# Revit family: CENTUM Isoliersattel für Rollenlager
name_source: partatom
category: HLS-Bauteile
revit_build: Autodesk Revit 2017 (Build: 20190507_1515(x64)
units: mm (PartAtom-declared; Revit-internal decimal feet)

## family parameters
Arbeitsebenenbasiert = Ja
Beim Laden mit Abzugskörper schneiden = Nein
Bemaßung runder Anschluss = Durchmesser verwenden
Gemeinsam genutzt = Ja
Immer vertikal = Nein
Raumberechnungspunkt = Nein
Teiletyp = Normal

## types (150) — shared parameters
Bauart = Auflagesattel
Fabrikat = MEFA
Firma = MEFA Befestigungs- und Montagesysteme GmbH
Isoliersattel = MEFA Isoliersattel 508 Isolierstärke  80
Länge Unterbau = 300 mm
Material = Stahl
Materialname = S235
Mengeneinheit = St
Verschluss = Mutter / Verschluss-Schraube
Vorgabe-Ansicht = 1219 mm
vpe = 1 St

## per-type parameters (varying)
| type | Artikelnummer | Breite Schellenband | Durchmesser Rollenauflage | EAN | Gewicht | Gewicht pro Bauteil | Kurztext1 | Kurztext2 | Oberflaeche | Rohraußendurchmesser | Stärke Material | Stärke Schellenband | Verschluss-Schraube | für Dämmstärke |
| CENTUM Isoliersattel für Rollenlager 219 Iso  50, fvz | 149afae0219 | 60 mm | 320 mm | 4250928433459 | 9.87 kg | 9.87 kg | Isoliersattel 219 60 x 6 mm | für Iso 50 mm fsv | feuerstückverzinkt | 219 mm  [stored 0.718504 ft] | 6 mm  [stored 0.019685 ft] | 6 mm | M16x60 | 50 mm |
| CENTUM Isoliersattel für Rollenlager 219 Iso  50, gvz | 149agae0219 | 60 mm | 320 mm | 4250928433954 | 9.29 kg | 9.29 kg | Isoliersattel 219 60 x 6 mm | für Iso 50 mm gvz | galvanisch verzinkt | 219 mm  [stored 0.718504 ft] | 6 mm  [stored 0.019685 ft] | 6 mm | M16x55 | 50 mm |
| CENTUM Isoliersattel für Rollenlager 219 Iso  50, roh | 149arae0219 | 60 mm | 320 mm | 4250928434456 | 9.29 kg | 9.29 kg | Isoliersattel 219 60 x 6 mm | für Iso 50 mm roh | roh | 219 mm  [stored 0.718504 ft] | 6 mm  [stored 0.019685 ft] | 6 mm | M16x55 | 50 mm |
| CENTUM Isoliersattel für Rollenlager 219 Iso  80, fvz | 149afah0219 | 60 mm | 380 mm | 4250928433558 | 11.30 kg | 11.30 kg | Isoliersattel 219 60 x 6 mm | für Iso 80 mm fsv | feuerstückverzinkt | 219 mm  [stored 0.718504 ft] | 6 mm  [stored 0.019685 ft] | 6 mm | M16x60 | 80 mm |
| CENTUM Isoliersattel für Rollenlager 219 Iso  80, gvz | 149agah0219 | 60 mm | 380 mm | 4250928434050 | 10.65 kg | 10.65 kg | Isoliersattel 219 60 x 6 mm | für Iso 80 mm gvz | galvanisch verzinkt | 219 mm  [stored 0.718504 ft] | 6 mm  [stored 0.019685 ft] | 6 mm | M16x55 | 80 mm |
| CENTUM Isoliersattel für Rollenlager 219 Iso  80, roh | 149arah0219 | 60 mm | 380 mm | 4250928434555 | 10.65 kg | 10.65 kg | Isoliersattel 219 60 x 6 mm | für Iso 80 mm roh | roh | 219 mm  [stored 0.718504 ft] | 6 mm  [stored 0.019685 ft] | 6 mm | M16x55 | 80 mm |
| CENTUM Isoliersattel für Rollenlager 219 Iso 100, fvz | 149afak0219 | 60 mm | 420 mm | 4250928433657 | 12.26 kg | 12.26 kg | Isoliersattel 219 60 x 6 mm | für Iso 100 mm fsv | feuerstückverzinkt | 219 mm  [stored 0.718504 ft] | 6 mm  [stored 0.019685 ft] | 6 mm | M16x60 | 100 mm |
| CENTUM Isoliersattel für Rollenlager 219 Iso 100, gvz | 149agak0219 | 60 mm | 420 mm | 4250928434159 | 11.55 kg | 11.55 kg | Isoliersattel 219 60 x 6 mm | für Iso 100 mm gvz | galvanisch verzinkt | 219 mm  [stored 0.718504 ft] | 6 mm  [stored 0.019685 ft] | 6 mm | M16x55 | 100 mm |
| CENTUM Isoliersattel für Rollenlager 219 Iso 100, roh | 149arak0219 | 60 mm | 420 mm | 4250928434654 | 11.55 kg | 11.55 kg | Isoliersattel 219 60 x 6 mm | für Iso 100 mm roh | roh | 219 mm  [stored 0.718504 ft] | 6 mm  [stored 0.019685 ft] | 6 mm | M16x55 | 100 mm |
| CENTUM Isoliersattel für Rollenlager 219 Iso 120, fvz | 149afam0219 | 60 mm | 460 mm | 4250928433756 | 13.22 kg | 13.22 kg | Isoliersattel 219 60 x 6 mm | für Iso 120 mm fsv | feuerstückverzinkt | 219 mm  [stored 0.718504 ft] | 6 mm  [stored 0.019685 ft] | 6 mm | M16x60 | 120 mm |
| CENTUM Isoliersattel für Rollenlager 219 Iso 120, gvz | 149agam0219 | 60 mm | 460 mm | 4250928434258 | 12.45 kg | 12.45 kg | Isoliersattel 219 60 x 6 mm | für Iso 120 mm gvz | galvanisch verzinkt | 219 mm  [stored 0.718504 ft] | 6 mm  [stored 0.019685 ft] | 6 mm | M16x55 | 120 mm |
| CENTUM Isoliersattel für Rollenlager 219 Iso 120, roh | 149aram0219 | 60 mm | 460 mm | 4250928434753 | 12.45 kg | 12.45 kg | Isoliersattel 219 60 x 6 mm | für Iso 120 mm roh | roh | 219 mm  [stored 0.718504 ft] | 6 mm  [stored 0.019685 ft] | 6 mm | M16x55 | 120 mm |
| CENTUM Isoliersattel für Rollenlager 219 Iso 150, fvz | 149afap0219 | 60 mm | 520 mm | 4250928433855 | 14.66 kg | 14.66 kg | Isoliersattel 219 60 x 6 mm | für Iso 150 mm fsv | feuerstückverzinkt | 219 mm  [stored 0.718504 ft] | 6 mm  [stored 0.019685 ft] | 6 mm | M16x60 | 150 mm |
| CENTUM Isoliersattel für Rollenlager 219 Iso 150, gvz | 149agap0219 | 60 mm | 520 mm | 4250928434357 | 13.82 kg | 13.82 kg | Isoliersattel 219 60 x 6 mm | für Iso 150 mm gvz | galvanisch verzinkt | 219 mm  [stored 0.718504 ft] | 6 mm  [stored 0.019685 ft] | 6 mm | M16x55 | 150 mm |
| CENTUM Isoliersattel für Rollenlager 219 Iso 150, roh | 149arap0219 | 60 mm | 520 mm | 4250928434852 | 13.82 kg | 13.82 kg | Isoliersattel 219 60 x 6 mm | für Iso 150 mm roh | roh | 219 mm  [stored 0.718504 ft] | 6 mm  [stored 0.019685 ft] | 6 mm | M16x55 | 150 mm |
| CENTUM Isoliersattel für Rollenlager 273 Iso  50, fvz | 149afae0273 | 60 mm | 375 mm | 4250928433466 | 12.61 kg | 12.61 kg | Isoliersattel 273 60 x 6 mm | für Iso 50 mm fsv | feuerstückverzinkt | 273 mm  [stored 0.895669 ft] | 8 mm  [stored 0.0262467 ft] | 6 mm | M16x60 | 50 mm |
| CENTUM Isoliersattel für Rollenlager 273 Iso  50, gvz | 149agae0273 | 60 mm | 375 mm | 4250928433961 | 11.95 kg | 11.95 kg | Isoliersattel 273 60 x 6 mm | für Iso 50 mm gvz | galvanisch verzinkt | 273 mm  [stored 0.895669 ft] | 8 mm  [stored 0.0262467 ft] | 6 mm | M16x55 | 50 mm |
| CENTUM Isoliersattel für Rollenlager 273 Iso  50, roh | 149arae0273 | 60 mm | 375 mm | 4250928434463 | 11.95 kg | 11.95 kg | Isoliersattel 273 60 x 6 mm | für Iso 50 mm roh | roh | 273 mm  [stored 0.895669 ft] | 8 mm  [stored 0.0262467 ft] | 6 mm | M16x55 | 50 mm |
| CENTUM Isoliersattel für Rollenlager 273 Iso  80, fvz | 149afah0273 | 60 mm | 435 mm | 4250928433565 | 14.51 kg | 14.51 kg | Isoliersattel 273 60 x 6 mm | für Iso 80 mm fsv | feuerstückverzinkt | 273 mm  [stored 0.895669 ft] | 8 mm  [stored 0.0262467 ft] | 6 mm | M16x60 | 80 mm |
| CENTUM Isoliersattel für Rollenlager 273 Iso  80, gvz | 149agah0273 | 60 mm | 435 mm | 4250928434067 | 13.76 kg | 13.76 kg | Isoliersattel 273 60 x 6 mm | für Iso 80 mm gvz | galvanisch verzinkt | 273 mm  [stored 0.895669 ft] | 8 mm  [stored 0.0262467 ft] | 6 mm | M16x55 | 80 mm |
| CENTUM Isoliersattel für Rollenlager 273 Iso  80, roh | 149arah0273 | 60 mm | 435 mm | 4250928434562 | 13.76 kg | 13.76 kg | Isoliersattel 273 60 x 6 mm | für Iso 80 mm roh | roh | 273 mm  [stored 0.895669 ft] | 8 mm  [stored 0.0262467 ft] | 6 mm | M16x55 | 80 mm |
| CENTUM Isoliersattel für Rollenlager 273 Iso 100, fvz | 149afak0273 | 60 mm | 475 mm | 4250928433664 | 15.78 kg | 15.78 kg | Isoliersattel 273 60 x 6 mm | für Iso 100 mm fsv | feuerstückverzinkt | 273 mm  [stored 0.895669 ft] | 8 mm  [stored 0.0262467 ft] | 6 mm | M16x60 | 100 mm |
| CENTUM Isoliersattel für Rollenlager 273 Iso 100, gvz | 149agak0273 | 60 mm | 475 mm | 4250928434166 | 14.98 kg | 14.98 kg | Isoliersattel 273 60 x 6 mm | für Iso 100 mm gvz | galvanisch verzinkt | 273 mm  [stored 0.895669 ft] | 8 mm  [stored 0.0262467 ft] | 6 mm | M16x55 | 100 mm |
| CENTUM Isoliersattel für Rollenlager 273 Iso 100, roh | 149arak0273 | 60 mm | 475 mm | 4250928434661 | 14.98 kg | 14.98 kg | Isoliersattel 273 60 x 6 mm | für Iso 100 mm roh | roh | 273 mm  [stored 0.895669 ft] | 8 mm  [stored 0.0262467 ft] | 6 mm | M16x55 | 100 mm |
| CENTUM Isoliersattel für Rollenlager 273 Iso 120, fvz | 149afam0273 | 60 mm | 515 mm | 4250928433763 | 17.04 kg | 17.04 kg | Isoliersattel 273 60 x 6 mm | für Iso 120 mm fsv | feuerstückverzinkt | 273 mm  [stored 0.895669 ft] | 8 mm  [stored 0.0262467 ft] | 6 mm | M16x60 | 120 mm |
| CENTUM Isoliersattel für Rollenlager 273 Iso 120, gvz | 149agam0273 | 60 mm | 515 mm | 4250928434265 | 16.19 kg | 16.19 kg | Isoliersattel 273 60 x 6 mm | für Iso 120 mm gvz | galvanisch verzinkt | 273 mm  [stored 0.895669 ft] | 8 mm  [stored 0.0262467 ft] | 6 mm | M16x55 | 120 mm |
| CENTUM Isoliersattel für Rollenlager 273 Iso 120, roh | 149aram0273 | 60 mm | 515 mm | 4250928434760 | 16.19 kg | 16.19 kg | Isoliersattel 273 60 x 6 mm | für Iso 120 mm roh | roh | 273 mm  [stored 0.895669 ft] | 8 mm  [stored 0.0262467 ft] | 6 mm | M16x55 | 120 mm |
| CENTUM Isoliersattel für Rollenlager 273 Iso 150, fvz | 149afap0273 | 60 mm | 575 mm | 4250928433862 | 18.92 kg | 18.92 kg | Isoliersattel 273 60 x 6 mm | für Iso 150 mm fsv | feuerstückverzinkt | 273 mm  [stored 0.895669 ft] | 8 mm  [stored 0.0262467 ft] | 6 mm | M16x60 | 150 mm |
| CENTUM Isoliersattel für Rollenlager 273 Iso 150, gvz | 149agap0273 | 60 mm | 575 mm | 4250928434364 | 17.98 kg | 17.98 kg | Isoliersattel 273 60 x 6 mm | für Iso 150 mm gvz | galvanisch verzinkt | 273 mm  [stored 0.895669 ft] | 8 mm  [stored 0.0262467 ft] | 6 mm | M16x55 | 150 mm |
| CENTUM Isoliersattel für Rollenlager 273 Iso 150, roh | 149arap0273 | 60 mm | 575 mm | 4250928434869 | 17.98 kg | 17.98 kg | Isoliersattel 273 60 x 6 mm | für Iso 150 mm roh | roh | 273 mm  [stored 0.895669 ft] | 8 mm  [stored 0.0262467 ft] | 6 mm | M16x55 | 150 mm |
| CENTUM Isoliersattel für Rollenlager 324 Iso  50, fvz | 149afae0324 | 60 mm | 425 mm | 4250928433473 | 15.42 kg | 15.42 kg | Isoliersattel 324 60 x 6 mm | für Iso 50 mm fsv | feuerstückverzinkt | 324 mm  [stored 1.06299 ft] | 10 mm  [stored 0.0328084 ft] | 6 mm | M16x60 | 50 mm |
| CENTUM Isoliersattel für Rollenlager 324 Iso  50, gvz | 149agae0324 | 60 mm | 425 mm | 4250928433978 | 14.68 kg | 14.68 kg | Isoliersattel 324 60 x 6 mm | für Iso 50 mm gvz | galvanisch verzinkt | 324 mm  [stored 1.06299 ft] | 10 mm  [stored 0.0328084 ft] | 6 mm | M16x55 | 50 mm |
| CENTUM Isoliersattel für Rollenlager 324 Iso  50, roh | 149arae0324 | 60 mm | 425 mm | 4250928434470 | 14.68 kg | 14.68 kg | Isoliersattel 324 60 x 6 mm | für Iso 50 mm roh | roh | 324 mm  [stored 1.06299 ft] | 10 mm  [stored 0.0328084 ft] | 6 mm | M16x55 | 50 mm |
| CENTUM Isoliersattel für Rollenlager 324 Iso  80, fvz | 149afah0324 | 60 mm | 485 mm | 4250928433572 | 17.77 kg | 17.77 kg | Isoliersattel 324 60 x 6 mm | für Iso 80 mm fsv | feuerstückverzinkt | 324 mm  [stored 1.06299 ft] | 10 mm  [stored 0.0328084 ft] | 6 mm | M16x60 | 80 mm |
| CENTUM Isoliersattel für Rollenlager 324 Iso  80, gvz | 149agah0324 | 60 mm | 485 mm | 4250928434074 | 16.95 kg | 16.95 kg | Isoliersattel 324 60 x 6 mm | für Iso 80 mm gvz | galvanisch verzinkt | 324 mm  [stored 1.06299 ft] | 10 mm  [stored 0.0328084 ft] | 6 mm | M16x55 | 80 mm |
| CENTUM Isoliersattel für Rollenlager 324 Iso  80, roh | 149arah0324 | 60 mm | 485 mm | 4250928434579 | 16.95 kg | 16.95 kg | Isoliersattel 324 60 x 6 mm | für Iso 80 mm roh | roh | 324 mm  [stored 1.06299 ft] | 10 mm  [stored 0.0328084 ft] | 6 mm | M16x55 | 80 mm |
| CENTUM Isoliersattel für Rollenlager 324 Iso 100, fvz | 149afak0324 | 60 mm | 525 mm | 4250928433671 | 19.33 kg | 19.33 kg | Isoliersattel 324 60 x 6 mm | für Iso 100 mm fsv | feuerstückverzinkt | 324 mm  [stored 1.06299 ft] | 10 mm  [stored 0.0328084 ft] | 6 mm | M16x60 | 100 mm |
| CENTUM Isoliersattel für Rollenlager 324 Iso 100, gvz | 149agak0324 | 60 mm | 525 mm | 4250928434173 | 18.48 kg | 18.48 kg | Isoliersattel 324 60 x 6 mm | für Iso 100 mm gvz | galvanisch verzinkt | 324 mm  [stored 1.06299 ft] | 10 mm  [stored 0.0328084 ft] | 6 mm | M16x55 | 100 mm |
| CENTUM Isoliersattel für Rollenlager 324 Iso 100, roh | 149arak0324 | 60 mm | 525 mm | 4250928434678 | 18.48 kg | 18.48 kg | Isoliersattel 324 60 x 6 mm | für Iso 100 mm roh | roh | 324 mm  [stored 1.06299 ft] | 10 mm  [stored 0.0328084 ft] | 6 mm | M16x55 | 100 mm |
| CENTUM Isoliersattel für Rollenlager 324 Iso 120, fvz | 149afam0324 | 60 mm | 565 mm | 4250928433770 | 20.90 kg | 20.90 kg | Isoliersattel 324 60 x 6 mm | für Iso 120 mm fsv | feuerstückverzinkt | 324 mm  [stored 1.06299 ft] | 10 mm  [stored 0.0328084 ft] | 6 mm | M16x60 | 120 mm |
| CENTUM Isoliersattel für Rollenlager 324 Iso 120, gvz | 149agam0324 | 60 mm | 565 mm | 4250928434272 | 19.96 kg | 19.96 kg | Isoliersattel 324 60 x 6 mm | für Iso 120 mm gvz | galvanisch verzinkt | 324 mm  [stored 1.06299 ft] | 10 mm  [stored 0.0328084 ft] | 6 mm | M16x55 | 120 mm |
| CENTUM Isoliersattel für Rollenlager 324 Iso 120, roh | 149aram0324 | 60 mm | 565 mm | 4250928434777 | 19.96 kg | 19.96 kg | Isoliersattel 324 60 x 6 mm | für Iso 120 mm roh | roh | 324 mm  [stored 1.06299 ft] | 10 mm  [stored 0.0328084 ft] | 6 mm | M16x55 | 120 mm |
| CENTUM Isoliersattel für Rollenlager 324 Iso 150, fvz | 149afap0324 | 60 mm | 625 mm | 4250928433879 | 23.24 kg | 23.24 kg | Isoliersattel 324 60 x 6 mm | für Iso 150 mm fsv | feuerstückverzinkt | 324 mm  [stored 1.06299 ft] | 10 mm  [stored 0.0328084 ft] | 6 mm | M16x60 | 150 mm |
| CENTUM Isoliersattel für Rollenlager 324 Iso 150, gvz | 149agap0324 | 60 mm | 625 mm | 4250928434371 | 22.23 kg | 22.23 kg | Isoliersattel 324 60 x 6 mm | für Iso 150 mm gvz | galvanisch verzinkt | 324 mm  [stored 1.06299 ft] | 10 mm  [stored 0.0328084 ft] | 6 mm | M16x55 | 150 mm |
| CENTUM Isoliersattel für Rollenlager 324 Iso 150, roh | 149arap0324 | 60 mm | 625 mm | 4250928434876 | 22.23 kg | 22.23 kg | Isoliersattel 324 60 x 6 mm | für Iso 150 mm roh | roh | 324 mm  [stored 1.06299 ft] | 10 mm  [stored 0.0328084 ft] | 6 mm | M16x55 | 150 mm |
| CENTUM Isoliersattel für Rollenlager 356 Iso  50, fvz | 149afae0356 | 60 mm | 460 mm | 4250928433480 | 20.41 kg | 20.41 kg | Isoliersattel 356 60 x 8 mm | für Iso 50 mm fsv | feuerstückverzinkt | 356 mm  [stored 1.16798 ft] | 12 mm  [stored 0.0393701 ft] | 8 mm | M16x60 | 50 mm |
| CENTUM Isoliersattel für Rollenlager 356 Iso  50, gvz | 149agae0356 | 60 mm | 460 mm | 4250928433985 | 19.59 kg | 19.59 kg | Isoliersattel 356 60 x 8 mm | für Iso 50 mm gvz | galvanisch verzinkt | 356 mm  [stored 1.16798 ft] | 12 mm  [stored 0.0393701 ft] | 8 mm | M16x55 | 50 mm |
| CENTUM Isoliersattel für Rollenlager 356 Iso  50, roh | 149arae0356 | 60 mm | 460 mm | 4250928434487 | 19.59 kg | 19.59 kg | Isoliersattel 356 60 x 8 mm | für Iso 50 mm roh | roh | 356 mm  [stored 1.16798 ft] | 12 mm  [stored 0.0393701 ft] | 8 mm | M16x55 | 50 mm |
| CENTUM Isoliersattel für Rollenlager 356 Iso  80, fvz | 149afah0356 | 60 mm | 520 mm | 4250928433589 | 23.21 kg | 23.21 kg | Isoliersattel 356 60 x 8 mm | für Iso 80 mm fsv | feuerstückverzinkt | 356 mm  [stored 1.16798 ft] | 12 mm  [stored 0.0393701 ft] | 8 mm | M16x60 | 80 mm |
| CENTUM Isoliersattel für Rollenlager 356 Iso  80, gvz | 149agah0356 | 60 mm | 520 mm | 4250928434081 | 22.31 kg | 22.31 kg | Isoliersattel 356 60 x 8 mm | für Iso 80 mm gvz | galvanisch verzinkt | 356 mm  [stored 1.16798 ft] | 12 mm  [stored 0.0393701 ft] | 8 mm | M16x55 | 80 mm |
| CENTUM Isoliersattel für Rollenlager 356 Iso  80, roh | 149arah0356 | 60 mm | 520 mm | 4250928434586 | 22.31 kg | 22.31 kg | Isoliersattel 356 60 x 8 mm | für Iso 80 mm roh | roh | 356 mm  [stored 1.16798 ft] | 12 mm  [stored 0.0393701 ft] | 8 mm | M16x55 | 80 mm |
| CENTUM Isoliersattel für Rollenlager 356 Iso 100, fvz | 149afak0356 | 60 mm | 560 mm | 4250928433688 | 25.08 kg | 25.08 kg | Isoliersattel 356 60 x 8 mm | für Iso 100 mm fsv | feuerstückverzinkt | 356 mm  [stored 1.16798 ft] | 12 mm  [stored 0.0393701 ft] | 8 mm | M16x60 | 100 mm |
| CENTUM Isoliersattel für Rollenlager 356 Iso 100, gvz | 149agak0356 | 60 mm | 560 mm | 4250928434180 | 24.13 kg | 24.13 kg | Isoliersattel 356 60 x 8 mm | für Iso 100 mm gvz | galvanisch verzinkt | 356 mm  [stored 1.16798 ft] | 12 mm  [stored 0.0393701 ft] | 8 mm | M16x55 | 100 mm |
| CENTUM Isoliersattel für Rollenlager 356 Iso 100, roh | 149arak0356 | 60 mm | 560 mm | 4250928434685 | 24.13 kg | 24.13 kg | Isoliersattel 356 60 x 8 mm | für Iso 100 mm roh | roh | 356 mm  [stored 1.16798 ft] | 12 mm  [stored 0.0393701 ft] | 8 mm | M16x55 | 100 mm |
| CENTUM Isoliersattel für Rollenlager 356 Iso 120, fvz | 149afam0356 | 60 mm | 600 mm | 4250928433787 | 26.94 kg | 26.94 kg | Isoliersattel 356 60 x 8 mm | für Iso 120 mm fsv | feuerstückverzinkt | 356 mm  [stored 1.16798 ft] | 12 mm  [stored 0.0393701 ft] | 8 mm | M16x60 | 120 mm |
| CENTUM Isoliersattel für Rollenlager 356 Iso 120, gvz | 149agam0356 | 60 mm | 600 mm | 4250928434289 | 25.93 kg | 25.93 kg | Isoliersattel 356 60 x 8 mm | für Iso 120 mm gvz | galvanisch verzinkt | 356 mm  [stored 1.16798 ft] | 12 mm  [stored 0.0393701 ft] | 8 mm | M16x55 | 120 mm |
| CENTUM Isoliersattel für Rollenlager 356 Iso 120, roh | 149aram0356 | 60 mm | 600 mm | 4250928434784 | 25.93 kg | 25.93 kg | Isoliersattel 356 60 x 8 mm | für Iso 120 mm roh | roh | 356 mm  [stored 1.16798 ft] | 12 mm  [stored 0.0393701 ft] | 8 mm | M16x55 | 120 mm |
| CENTUM Isoliersattel für Rollenlager 356 Iso 150, fvz | 149afap0356 | 60 mm | 660 mm | 4250928433886 | 29.74 kg | 29.74 kg | Isoliersattel 356 60 x 8 mm | für Iso 150 mm fsv | feuerstückverzinkt | 356 mm  [stored 1.16798 ft] | 12 mm  [stored 0.0393701 ft] | 8 mm | M16x60 | 150 mm |
| CENTUM Isoliersattel für Rollenlager 356 Iso 150, gvz | 149agap0356 | 60 mm | 660 mm | 4250928434388 | 28.65 kg | 28.65 kg | Isoliersattel 356 60 x 8 mm | für Iso 150 mm gvz | galvanisch verzinkt | 356 mm  [stored 1.16798 ft] | 12 mm  [stored 0.0393701 ft] | 8 mm | M16x55 | 150 mm |
| CENTUM Isoliersattel für Rollenlager 356 Iso 150, roh | 149arap0356 | 60 mm | 660 mm | 4250928434883 | 28.65 kg | 28.65 kg | Isoliersattel 356 60 x 8 mm | für Iso 150 mm roh | roh | 356 mm  [stored 1.16798 ft] | 12 mm  [stored 0.0393701 ft] | 8 mm | M16x55 | 150 mm |
| CENTUM Isoliersattel für Rollenlager 406 Iso  50, fvz | 149afae0406 | 60 mm | 510 mm | 4250928433497 | 22.54 kg | 22.54 kg | Isoliersattel 406 60 x 8 mm | für Iso 50 mm fsv | feuerstückverzinkt | 406 mm  [stored 1.33202 ft] | 12 mm  [stored 0.0393701 ft] | 8 mm | M16x60 | 50 mm |
| CENTUM Isoliersattel für Rollenlager 406 Iso  50, gvz | 149agae0406 | 60 mm | 510 mm | 4250928433992 | 21.64 kg | 21.64 kg | Isoliersattel 406 60 x 8 mm | für Iso 50 mm gvz | galvanisch verzinkt | 406 mm  [stored 1.33202 ft] | 12 mm  [stored 0.0393701 ft] | 8 mm | M16x55 | 50 mm |
| CENTUM Isoliersattel für Rollenlager 406 Iso  50, roh | 149arae0406 | 60 mm | 510 mm | 4250928434494 | 21.64 kg | 21.64 kg | Isoliersattel 406 60 x 8 mm | für Iso 50 mm roh | roh | 406 mm  [stored 1.33202 ft] | 12 mm  [stored 0.0393701 ft] | 8 mm | M16x55 | 50 mm |
| CENTUM Isoliersattel für Rollenlager 406 Iso  80, fvz | 149afah0406 | 60 mm | 570 mm | 4250928433596 | 25.27 kg | 25.27 kg | Isoliersattel 406 60 x 8 mm | für Iso 80 mm fsv | feuerstückverzinkt | 406 mm  [stored 1.33202 ft] | 12 mm  [stored 0.0393701 ft] | 8 mm | M16x60 | 80 mm |
| CENTUM Isoliersattel für Rollenlager 406 Iso  80, gvz | 149agah0406 | 60 mm | 570 mm | 4250928434098 | 24.37 kg | 24.37 kg | Isoliersattel 406 60 x 8 mm | für Iso 80 mm gvz | galvanisch verzinkt | 406 mm  [stored 1.33202 ft] | 12 mm  [stored 0.0393701 ft] | 8 mm | M16x55 | 80 mm |
| CENTUM Isoliersattel für Rollenlager 406 Iso  80, roh | 149arah0406 | 60 mm | 570 mm | 4250928434593 | 24.37 kg | 24.37 kg | Isoliersattel 406 60 x 8 mm | für Iso 80 mm roh | roh | 406 mm  [stored 1.33202 ft] | 12 mm  [stored 0.0393701 ft] | 8 mm | M16x55 | 80 mm |
| CENTUM Isoliersattel für Rollenlager 406 Iso 100, fvz | 149afak0406 | 60 mm | 610 mm | 4250928433695 | 27.21 kg | 27.21 kg | Isoliersattel 406 60 x 8 mm | für Iso 100 mm fsv | feuerstückverzinkt | 406 mm  [stored 1.33202 ft] | 12 mm  [stored 0.0393701 ft] | 8 mm | M16x60 | 100 mm |
| CENTUM Isoliersattel für Rollenlager 406 Iso 100, gvz | 149agak0406 | 60 mm | 610 mm | 4250928434197 | 26.17 kg | 26.17 kg | Isoliersattel 406 60 x 8 mm | für Iso 100 mm gvz | galvanisch verzinkt | 406 mm  [stored 1.33202 ft] | 12 mm  [stored 0.0393701 ft] | 8 mm | M16x55 | 100 mm |
| CENTUM Isoliersattel für Rollenlager 406 Iso 100, roh | 149arak0406 | 60 mm | 610 mm | 4250928434692 | 26.17 kg | 26.17 kg | Isoliersattel 406 60 x 8 mm | für Iso 100 mm roh | roh | 406 mm  [stored 1.33202 ft] | 12 mm  [stored 0.0393701 ft] | 8 mm | M16x55 | 100 mm |
| CENTUM Isoliersattel für Rollenlager 406 Iso 120, fvz | 149afam0406 | 60 mm | 650 mm | 4250928433794 | 29.08 kg | 29.08 kg | Isoliersattel 406 60 x 8 mm | für Iso 120 mm fsv | feuerstückverzinkt | 406 mm  [stored 1.33202 ft] | 12 mm  [stored 0.0393701 ft] | 8 mm | M16x60 | 120 mm |
| CENTUM Isoliersattel für Rollenlager 406 Iso 120, gvz | 149agam0406 | 60 mm | 650 mm | 4250928434296 | 27.98 kg | 27.98 kg | Isoliersattel 406 60 x 8 mm | für Iso 120 mm gvz | galvanisch verzinkt | 406 mm  [stored 1.33202 ft] | 12 mm  [stored 0.0393701 ft] | 8 mm | M16x55 | 120 mm |
| CENTUM Isoliersattel für Rollenlager 406 Iso 120, roh | 149aram0406 | 60 mm | 650 mm | 4250928434791 | 27.98 kg | 27.98 kg | Isoliersattel 406 60 x 8 mm | für Iso 120 mm roh | roh | 406 mm  [stored 1.33202 ft] | 12 mm  [stored 0.0393701 ft] | 8 mm | M16x55 | 120 mm |
| CENTUM Isoliersattel für Rollenlager 406 Iso 150, fvz | 149afap0406 | 60 mm | 710 mm | 4250928433893 | 31.88 kg | 31.88 kg | Isoliersattel 406 60 x 8 mm | für Iso 150 mm fsv | feuerstückverzinkt | 406 mm  [stored 1.33202 ft] | 12 mm  [stored 0.0393701 ft] | 8 mm | M16x60 | 150 mm |
| CENTUM Isoliersattel für Rollenlager 406 Iso 150, gvz | 149agap0406 | 60 mm | 710 mm | 4250928434395 | 30.70 kg | 30.70 kg | Isoliersattel 406 60 x 8 mm | für Iso 150 mm gvz | galvanisch verzinkt | 406 mm  [stored 1.33202 ft] | 12 mm  [stored 0.0393701 ft] | 8 mm | M16x55 | 150 mm |
| CENTUM Isoliersattel für Rollenlager 406 Iso 150, roh | 149arap0406 | 60 mm | 710 mm | 4250928434890 | 30.70 kg | 30.70 kg | Isoliersattel 406 60 x 8 mm | für Iso 150 mm roh | roh | 406 mm  [stored 1.33202 ft] | 12 mm  [stored 0.0393701 ft] | 8 mm | M16x55 | 150 mm |
| CENTUM Isoliersattel für Rollenlager 457 Iso  50, fvz | 149afae0457 | 60 mm | 560 mm | 4250928433503 | 26.83 kg | 26.83 kg | Isoliersattel 457 60 x 8 mm | für Iso 50 mm fsv | feuerstückverzinkt | 457 mm  [stored 1.49934 ft] | 15 mm  [stored 0.0492126 ft] | 8 mm | M16x60 | 50 mm |
| CENTUM Isoliersattel für Rollenlager 457 Iso  50, gvz | 149agae0457 | 60 mm | 560 mm | 4250928434005 | 25.85 kg | 25.85 kg | Isoliersattel 457 60 x 8 mm | für Iso 50 mm gvz | galvanisch verzinkt | 457 mm  [stored 1.49934 ft] | 15 mm  [stored 0.0492126 ft] | 8 mm | M16x55 | 50 mm |
| CENTUM Isoliersattel für Rollenlager 457 Iso  50, roh | 149arae0457 | 60 mm | 560 mm | 4250928434500 | 25.85 kg | 25.85 kg | Isoliersattel 457 60 x 8 mm | für Iso 50 mm roh | roh | 457 mm  [stored 1.49934 ft] | 15 mm  [stored 0.0492126 ft] | 8 mm | M16x55 | 50 mm |
| CENTUM Isoliersattel für Rollenlager 457 Iso  80, fvz | 149afah0457 | 60 mm | 620 mm | 4250928433602 | 30.33 kg | 30.33 kg | Isoliersattel 457 60 x 8 mm | für Iso 80 mm fsv | feuerstückverzinkt | 457 mm  [stored 1.49934 ft] | 15 mm  [stored 0.0492126 ft] | 8 mm | M16x60 | 80 mm |
| CENTUM Isoliersattel für Rollenlager 457 Iso  80, gvz | 149agah0457 | 60 mm | 620 mm | 4250928434104 | 29.26 kg | 29.26 kg | Isoliersattel 457 60 x 8 mm | für Iso 80 mm gvz | galvanisch verzinkt | 457 mm  [stored 1.49934 ft] | 15 mm  [stored 0.0492126 ft] | 8 mm | M16x55 | 80 mm |
| CENTUM Isoliersattel für Rollenlager 457 Iso  80, roh | 149arah0457 | 60 mm | 620 mm | 4250928434609 | 29.26 kg | 29.26 kg | Isoliersattel 457 60 x 8 mm | für Iso 80 mm roh | roh | 457 mm  [stored 1.49934 ft] | 15 mm  [stored 0.0492126 ft] | 8 mm | M16x55 | 80 mm |
| CENTUM Isoliersattel für Rollenlager 457 Iso 100, fvz | 149afak0457 | 60 mm | 660 mm | 4250928433701 | 32.64 kg | 32.64 kg | Isoliersattel 457 60 x 8 mm | für Iso 100 mm fsv | feuerstückverzinkt | 457 mm  [stored 1.49934 ft] | 15 mm  [stored 0.0492126 ft] | 8 mm | M16x60 | 100 mm |
| CENTUM Isoliersattel für Rollenlager 457 Iso 100, gvz | 149agak0457 | 60 mm | 660 mm | 4250928434203 | 31.52 kg | 31.52 kg | Isoliersattel 457 60 x 8 mm | für Iso 100 mm gvz | galvanisch verzinkt | 457 mm  [stored 1.49934 ft] | 15 mm  [stored 0.0492126 ft] | 8 mm | M16x55 | 100 mm |
| CENTUM Isoliersattel für Rollenlager 457 Iso 100, roh | 149arak0457 | 60 mm | 660 mm | 4250928434708 | 31.52 kg | 31.52 kg | Isoliersattel 457 60 x 8 mm | für Iso 100 mm roh | roh | 457 mm  [stored 1.49934 ft] | 15 mm  [stored 0.0492126 ft] | 8 mm | M16x55 | 100 mm |
| CENTUM Isoliersattel für Rollenlager 457 Iso 120, fvz | 149afam0457 | 60 mm | 700 mm | 4250928433800 | 34.96 kg | 34.96 kg | Isoliersattel 457 60 x 8 mm | für Iso 120 mm fsv | feuerstückverzinkt | 457 mm  [stored 1.49934 ft] | 15 mm  [stored 0.0492126 ft] | 8 mm | M16x60 | 120 mm |
| CENTUM Isoliersattel für Rollenlager 457 Iso 120, gvz | 149agam0457 | 60 mm | 700 mm | 4250928434302 | 33.79 kg | 33.79 kg | Isoliersattel 457 60 x 8 mm | für Iso 120 mm gvz | galvanisch verzinkt | 457 mm  [stored 1.49934 ft] | 15 mm  [stored 0.0492126 ft] | 8 mm | M16x55 | 120 mm |
| CENTUM Isoliersattel für Rollenlager 457 Iso 120, roh | 149aram0457 | 60 mm | 700 mm | 4250928434807 | 33.79 kg | 33.79 kg | Isoliersattel 457 60 x 8 mm | für Iso 120 mm roh | roh | 457 mm  [stored 1.49934 ft] | 15 mm  [stored 0.0492126 ft] | 8 mm | M16x55 | 120 mm |
| CENTUM Isoliersattel für Rollenlager 457 Iso 150, fvz | 149afap0457 | 60 mm | 760 mm | 4250928433909 | 38.44 kg | 38.44 kg | Isoliersattel 457 60 x 8 mm | für Iso 150 mm fsv | feuerstückverzinkt | 457 mm  [stored 1.49934 ft] | 15 mm  [stored 0.0492126 ft] | 8 mm | M16x60 | 150 mm |
| CENTUM Isoliersattel für Rollenlager 457 Iso 150, gvz | 149agap0457 | 60 mm | 760 mm | 4250928434401 | 37.18 kg | 37.18 kg | Isoliersattel 457 60 x 8 mm | für Iso 150 mm gvz | galvanisch verzinkt | 457 mm  [stored 1.49934 ft] | 15 mm  [stored 0.0492126 ft] | 8 mm | M16x55 | 150 mm |
| CENTUM Isoliersattel für Rollenlager 457 Iso 150, roh | 149arap0457 | 60 mm | 760 mm | 4250928434906 | 37.18 kg | 37.18 kg | Isoliersattel 457 60 x 8 mm | für Iso 150 mm roh | roh | 457 mm  [stored 1.49934 ft] | 15 mm  [stored 0.0492126 ft] | 8 mm | M16x55 | 150 mm |
| CENTUM Isoliersattel für Rollenlager 508 Iso  50, fvz | 149afae0508 | 70 mm | 610 mm | 4250928433510 | 36.48 kg | 36.48 kg | Isoliersattel 508 70 x 10 mm | für Iso 50 mm fsv | feuerstückverzinkt | 508 mm | 15 mm  [stored 0.0492126 ft] | 10 mm | M20x70 | 50 mm |
| CENTUM Isoliersattel für Rollenlager 508 Iso  50, gvz | 149agae0508 | 70 mm | 610 mm | 4250928434012 | 35.30 kg | 35.30 kg | Isoliersattel 508 70 x 10 mm | für Iso 50 mm gvz | galvanisch verzinkt | 508 mm | 15 mm  [stored 0.0492126 ft] | 10 mm | M20x70 | 50 mm |
| CENTUM Isoliersattel für Rollenlager 508 Iso  50, roh | 149arae0508 | 70 mm | 610 mm | 4250928434517 | 35.30 kg | 35.30 kg | Isoliersattel 508 70 x 10 mm | für Iso 50 mm roh | roh | 508 mm | 15 mm  [stored 0.0492126 ft] | 10 mm | M20x70 | 50 mm |
| CENTUM Isoliersattel für Rollenlager 508 Iso  80, fvz | 149afah0508 | 70 mm | 670 mm | 4250928433619 | 39.97 kg | 39.97 kg | Isoliersattel 508 70 x 10 mm | für Iso 80 mm fsv | feuerstückverzinkt | 508 mm | 15 mm  [stored 0.0492126 ft] | 10 mm | M20x70 | 80 mm |
| CENTUM Isoliersattel für Rollenlager 508 Iso  80, gvz | 149agah0508 | 70 mm | 670 mm | 4250928434111 | 38.71 kg | 38.71 kg | Isoliersattel 508 70 x 10 mm | für Iso 80 mm gvz | galvanisch verzinkt | 508 mm | 15 mm  [stored 0.0492126 ft] | 10 mm | M20x70 | 80 mm |
| CENTUM Isoliersattel für Rollenlager 508 Iso  80, roh | 149arah0508 | 70 mm | 670 mm | 4250928434616 | 38.71 kg | 38.71 kg | Isoliersattel 508 70 x 10 mm | für Iso 80 mm roh | roh | 508 mm | 15 mm  [stored 0.0492126 ft] | 10 mm | M20x70 | 80 mm |
| CENTUM Isoliersattel für Rollenlager 508 Iso 100, fvz | 149afak0508 | 70 mm | 710 mm | 4250928433718 | 42.28 kg | 42.28 kg | Isoliersattel 508 70 x 10 mm | für Iso 100 mm fsv | feuerstückverzinkt | 508 mm | 15 mm  [stored 0.0492126 ft] | 10 mm | M20x70 | 100 mm |
| CENTUM Isoliersattel für Rollenlager 508 Iso 100, gvz | 149agak0508 | 70 mm | 710 mm | 4250928434210 | 40.96 kg | 40.96 kg | Isoliersattel 508 70 x 10 mm | für Iso 100 mm gvz | galvanisch verzinkt | 508 mm | 15 mm  [stored 0.0492126 ft] | 10 mm | M20x70 | 100 mm |
| CENTUM Isoliersattel für Rollenlager 508 Iso 100, roh | 149arak0508 | 70 mm | 710 mm | 4250928434715 | 40.96 kg | 40.96 kg | Isoliersattel 508 70 x 10 mm | für Iso 100 mm roh | roh | 508 mm | 15 mm  [stored 0.0492126 ft] | 10 mm | M20x70 | 100 mm |
| CENTUM Isoliersattel für Rollenlager 508 Iso 120, fvz | 149afam0508 | 70 mm | 750 mm | 4250928433817 | 44.60 kg | 44.60 kg | Isoliersattel 508 70 x 10 mm | für Iso 120 mm fsv | feuerstückverzinkt | 508 mm | 15 mm  [stored 0.0492126 ft] | 10 mm | M20x70 | 120 mm |
| CENTUM Isoliersattel für Rollenlager 508 Iso 120, roh | 149aram0508 | 70 mm | 750 mm | 4250928434814 | 43.23 kg | 43.23 kg | Isoliersattel 508 70 x 10 mm | für Iso 120 mm roh | roh | 508 mm | 15 mm  [stored 0.0492126 ft] | 10 mm | M20x70 | 120 mm |
| CENTUM Isoliersattel für Rollenlager 508 Iso 120, gvz | 149agam0508 | 70 mm | 750 mm | 4250928434319 | 43.23 kg | 43.23 kg | Isoliersattel 508 70 x 10 mm | für Iso 120 mm gvz | galvanisch verzinkt | 508 mm | 15 mm  [stored 0.0492126 ft] | 10 mm | M20x70 | 120 mm |
| CENTUM Isoliersattel für Rollenlager 508 Iso 150, fvz | 149afap0508 | 70 mm | 810 mm | 4250928433916 | 48.12 kg | 48.12 kg | Isoliersattel 508 70 x 10 mm | für Iso 150 mm fsv | feuerstückverzinkt | 508 mm | 15 mm  [stored 0.0492126 ft] | 10 mm | M20x70 | 150 mm |
| CENTUM Isoliersattel für Rollenlager 508 Iso 150, gvz | 149agap0508 | 70 mm | 810 mm | 4250928434418 | 46.66 kg | 46.66 kg | Isoliersattel 508 70 x 10 mm | für Iso 150 mm gvz | galvanisch verzinkt | 508 mm | 15 mm  [stored 0.0492126 ft] | 10 mm | M20x70 | 150 mm |
| CENTUM Isoliersattel für Rollenlager 508 Iso 150, roh | 149arap0508 | 70 mm | 810 mm | 4250928434913 | 46.66 kg | 46.66 kg | Isoliersattel 508 70 x 10 mm | für Iso 150 mm roh | roh | 508 mm | 15 mm  [stored 0.0492126 ft] | 10 mm | M20x70 | 150 mm |
| CENTUM Isoliersattel für Rollenlager 610 Iso  50, fvz | 149afae0610 | 70 mm | 710 mm | 4250928433527 | 42.20 kg | 42.20 kg | Isoliersattel 610 70 x 10 mm | für Iso 50 mm fsv | feuerstückverzinkt | 610 mm  [stored 2.00131 ft] | 15 mm  [stored 0.0492126 ft] | 10 mm | M20x70 | 50 mm |
| CENTUM Isoliersattel für Rollenlager 610 Iso  50, gvz | 149agae0610 | 70 mm | 710 mm | 4250928434029 | 40.83 kg | 40.83 kg | Isoliersattel 610 70 x 10 mm | für Iso 50 mm gvz | galvanisch verzinkt | 610 mm  [stored 2.00131 ft] | 15 mm  [stored 0.0492126 ft] | 10 mm | M20x70 | 50 mm |
| CENTUM Isoliersattel für Rollenlager 610 Iso  50, roh | 149arae0610 | 70 mm | 710 mm | 4250928434524 | 40.83 kg | 40.83 kg | Isoliersattel 610 70 x 10 mm | für Iso 50 mm roh | roh | 610 mm  [stored 2.00131 ft] | 15 mm  [stored 0.0492126 ft] | 10 mm | M20x70 | 50 mm |
| CENTUM Isoliersattel für Rollenlager 610 Iso  80, fvz | 149afah0610 | 70 mm | 770 mm | 4250928433626 | 45.68 kg | 45.68 kg | Isoliersattel 610 70 x 10 mm | für Iso 80 mm fsv | feuerstückverzinkt | 610 mm  [stored 2.00131 ft] | 15 mm  [stored 0.0492126 ft] | 10 mm | M20x70 | 80 mm |
| CENTUM Isoliersattel für Rollenlager 610 Iso  80, gvz | 149agah0610 | 70 mm | 770 mm | 4250928434128 | 44.23 kg | 44.23 kg | Isoliersattel 610 70 x 10 mm | für Iso 80 mm gvz | galvanisch verzinkt | 610 mm  [stored 2.00131 ft] | 15 mm  [stored 0.0492126 ft] | 10 mm | M20x70 | 80 mm |
| CENTUM Isoliersattel für Rollenlager 610 Iso  80, roh | 149arah0610 | 70 mm | 770 mm | 4250928434623 | 44.23 kg | 44.23 kg | Isoliersattel 610 70 x 10 mm | für Iso 80 mm roh | roh | 610 mm  [stored 2.00131 ft] | 15 mm  [stored 0.0492126 ft] | 10 mm | M20x70 | 80 mm |
| CENTUM Isoliersattel für Rollenlager 610 Iso 100, fvz | 149afak0610 | 70 mm | 810 mm | 4250928433725 | 48.00 kg | 48.00 kg | Isoliersattel 610 70 x 10 mm | für Iso 100 mm fsv | feuerstückverzinkt | 610 mm  [stored 2.00131 ft] | 15 mm  [stored 0.0492126 ft] | 10 mm | M20x70 | 100 mm |
| CENTUM Isoliersattel für Rollenlager 610 Iso 100, gvz | 149agak0610 | 70 mm | 810 mm | 4250928434227 | 46.50 kg | 46.50 kg | Isoliersattel 610 70 x 10 mm | für Iso 100 mm gvz | galvanisch verzinkt | 610 mm  [stored 2.00131 ft] | 15 mm  [stored 0.0492126 ft] | 10 mm | M20x70 | 100 mm |
| CENTUM Isoliersattel für Rollenlager 610 Iso 100, roh | 149arak0610 | 70 mm | 810 mm | 4250928434722 | 46.50 kg | 46.50 kg | Isoliersattel 610 70 x 10 mm | für Iso 100 mm roh | roh | 610 mm  [stored 2.00131 ft] | 15 mm  [stored 0.0492126 ft] | 10 mm | M20x70 | 100 mm |
| CENTUM Isoliersattel für Rollenlager 610 Iso 120, fvz | 149afam0610 | 70 mm | 850 mm | 4250928433824 | 50.33 kg | 50.33 kg | Isoliersattel 610 70 x 10 mm | für Iso 120 mm fsv | feuerstückverzinkt | 610 mm  [stored 2.00131 ft] | 15 mm  [stored 0.0492126 ft] | 10 mm | M20x70 | 120 mm |
| CENTUM Isoliersattel für Rollenlager 610 Iso 120, gvz | 149agam0610 | 70 mm | 850 mm | 4250928434326 | 48.76 kg | 48.76 kg | Isoliersattel 610 70 x 10 mm | für Iso 120 mm gvz | galvanisch verzinkt | 610 mm  [stored 2.00131 ft] | 15 mm  [stored 0.0492126 ft] | 10 mm | M20x70 | 120 mm |
| CENTUM Isoliersattel für Rollenlager 610 Iso 120, roh | 149aram0610 | 70 mm | 850 mm | 4250928434821 | 48.76 kg | 48.76 kg | Isoliersattel 610 70 x 10 mm | für Iso 120 mm roh | roh | 610 mm  [stored 2.00131 ft] | 15 mm  [stored 0.0492126 ft] | 10 mm | M20x70 | 120 mm |
| CENTUM Isoliersattel für Rollenlager 610 Iso 150, fvz | 149afap0610 | 70 mm | 910 mm | 4250928433923 | 53.82 kg | 53.82 kg | Isoliersattel 610 70 x 10 mm | für Iso 150 mm fsv | feuerstückverzinkt | 610 mm  [stored 2.00131 ft] | 15 mm  [stored 0.0492126 ft] | 10 mm | M20x70 | 150 mm |
| CENTUM Isoliersattel für Rollenlager 610 Iso 150, gvz | 149agap0610 | 70 mm | 910 mm | 4250928434425 | 52.18 kg | 52.18 kg | Isoliersattel 610 70 x 10 mm | für Iso 150 mm gvz | galvanisch verzinkt | 610 mm  [stored 2.00131 ft] | 15 mm  [stored 0.0492126 ft] | 10 mm | M20x70 | 150 mm |
| CENTUM Isoliersattel für Rollenlager 610 Iso 150, roh | 149arap0610 | 70 mm | 910 mm | 4250928434920 | 52.18 kg | 52.18 kg | Isoliersattel 610 70 x 10 mm | für Iso 150 mm roh | roh | 610 mm  [stored 2.00131 ft] | 15 mm  [stored 0.0492126 ft] | 10 mm | M20x70 | 150 mm |
| CENTUM Isoliersattel für Rollenlager 711 Iso  50, fvz | 149afae0711 | 70 mm | 815 mm | 4250928433534 | 48.26 kg | 48.26 kg | Isoliersattel 711 70 x 10 mm | für Iso 50 mm fsv | feuerstückverzinkt | 711 mm  [stored 2.33268 ft] | 15 mm  [stored 0.0492126 ft] | 10 mm | M20x70 | 50 mm |
| CENTUM Isoliersattel für Rollenlager 711 Iso  50, gvz | 149agae0711 | 70 mm | 815 mm | 4250928434036 | 46.70 kg | 46.70 kg | Isoliersattel 711 70 x 10 mm | für Iso 50 mm gvz | galvanisch verzinkt | 711 mm  [stored 2.33268 ft] | 15 mm  [stored 0.0492126 ft] | 10 mm | M20x70 | 50 mm |
| CENTUM Isoliersattel für Rollenlager 711 Iso  50, roh | 149arae0711 | 70 mm | 815 mm | 4250928434531 | 46.70 kg | 46.70 kg | Isoliersattel 711 70 x 10 mm | für Iso 50 mm roh | roh | 711 mm  [stored 2.33268 ft] | 15 mm  [stored 0.0492126 ft] | 10 mm | M20x70 | 50 mm |
| CENTUM Isoliersattel für Rollenlager 711 Iso  80, fvz | 149afah0711 | 70 mm | 875 mm | 4250928433633 | 51.75 kg | 51.75 kg | Isoliersattel 711 70 x 10 mm | für Iso 80 mm fsv | feuerstückverzinkt | 711 mm  [stored 2.33268 ft] | 15 mm  [stored 0.0492126 ft] | 10 mm | M20x70 | 80 mm |
| CENTUM Isoliersattel für Rollenlager 711 Iso  80, gvz | 149agah0711 | 70 mm | 875 mm | 4250928434135 | 50.10 kg | 50.10 kg | Isoliersattel 711 70 x 10 mm | für Iso 80 mm gvz | galvanisch verzinkt | 711 mm  [stored 2.33268 ft] | 15 mm  [stored 0.0492126 ft] | 10 mm | M20x70 | 80 mm |
| CENTUM Isoliersattel für Rollenlager 711 Iso  80, roh | 149arah0711 | 70 mm | 875 mm | 4250928434630 | 50.10 kg | 50.10 kg | Isoliersattel 711 70 x 10 mm | für Iso 80 mm roh | roh | 711 mm  [stored 2.33268 ft] | 15 mm  [stored 0.0492126 ft] | 10 mm | M20x70 | 80 mm |
| CENTUM Isoliersattel für Rollenlager 711 Iso 100, fvz | 149afak0711 | 70 mm | 915 mm | 4250928433732 | 54.07 kg | 54.07 kg | Isoliersattel 711 70 x 10 mm | für Iso 100 mm fsv | feuerstückverzinkt | 711 mm  [stored 2.33268 ft] | 15 mm  [stored 0.0492126 ft] | 10 mm | M20x70 | 100 mm |
| CENTUM Isoliersattel für Rollenlager 711 Iso 100, gvz | 149agak0711 | 70 mm | 915 mm | 4250928434234 | 52.37 kg | 52.37 kg | Isoliersattel 711 70 x 10 mm | für Iso 100 mm gvz | galvanisch verzinkt | 711 mm  [stored 2.33268 ft] | 15 mm  [stored 0.0492126 ft] | 10 mm | M20x70 | 100 mm |
| CENTUM Isoliersattel für Rollenlager 711 Iso 100, roh | 149arak0711 | 70 mm | 915 mm | 4250928434739 | 52.37 kg | 52.37 kg | Isoliersattel 711 70 x 10 mm | für Iso 100 mm roh | roh | 711 mm  [stored 2.33268 ft] | 15 mm  [stored 0.0492126 ft] | 10 mm | M20x70 | 100 mm |
| CENTUM Isoliersattel für Rollenlager 711 Iso 120, fvz | 149afam0711 | 70 mm | 955 mm | 4250928433831 | 56.40 kg | 56.40 kg | Isoliersattel 711 70 x 10 mm | für Iso 120 mm fsv | feuerstückverzinkt | 711 mm  [stored 2.33268 ft] | 15 mm  [stored 0.0492126 ft] | 10 mm | M20x70 | 120 mm |
| CENTUM Isoliersattel für Rollenlager 711 Iso 120, gvz | 149agam0711 | 70 mm | 955 mm | 4250928434333 | 54.63 kg | 54.63 kg | Isoliersattel 711 70 x 10 mm | für Iso 120 mm gvz | galvanisch verzinkt | 711 mm  [stored 2.33268 ft] | 15 mm  [stored 0.0492126 ft] | 10 mm | M20x70 | 120 mm |
| CENTUM Isoliersattel für Rollenlager 711 Iso 120, roh | 149aram0711 | 70 mm | 955 mm | 4250928434838 | 54.63 kg | 54.63 kg | Isoliersattel 711 70 x 10 mm | für Iso 120 mm roh | roh | 711 mm  [stored 2.33268 ft] | 15 mm  [stored 0.0492126 ft] | 10 mm | M20x70 | 120 mm |
| CENTUM Isoliersattel für Rollenlager 711 Iso 150, fvz | 149afap0711 | 70 mm | 1.015 mm | 4250928433930 | 59.88 kg | 59.88 kg | Isoliersattel 711 70 x 10 mm | für Iso 150 mm fsv | feuerstückverzinkt | 711 mm  [stored 2.33268 ft] | 15 mm  [stored 0.0492126 ft] | 10 mm | M20x70 | 150 mm |
| CENTUM Isoliersattel für Rollenlager 711 Iso 150, gvz | 149agap0711 | 70 mm | 1.015 mm | 4250928434432 | 58.04 kg | 58.04 kg | Isoliersattel 711 70 x 10 mm | für Iso 150 mm gvz | galvanisch verzinkt | 711 mm  [stored 2.33268 ft] | 15 mm  [stored 0.0492126 ft] | 10 mm | M20x70 | 150 mm |
| CENTUM Isoliersattel für Rollenlager 711 Iso 150, roh | 149arap0711 | 70 mm | 1.015 mm | 4250928434937 | 58.04 kg | 58.04 kg | Isoliersattel 711 70 x 10 mm | für Iso 150 mm roh | roh | 711 mm  [stored 2.33268 ft] | 15 mm  [stored 0.0492126 ft] | 10 mm | M20x70 | 150 mm |
| CENTUM Isoliersattel für Rollenlager 813 Iso  50, fvz | 149afae0813 | 70 mm | 915 mm | 4250928433541 | 54.02 kg | 54.02 kg | Isoliersattel 813 70 x 10 mm | für Iso 50 mm fsv | feuerstückverzinkt | 813 mm | 15 mm  [stored 0.0492126 ft] | 10 mm | M20x70 | 50 mm |
| CENTUM Isoliersattel für Rollenlager 813 Iso  50, gvz | 149agae0813 | 70 mm | 915 mm | 4250928434043 | 52.26 kg | 52.26 kg | Isoliersattel 813 70 x 10 mm | für Iso 50 mm gvz | galvanisch verzinkt | 813 mm | 15 mm  [stored 0.0492126 ft] | 10 mm | M20x70 | 50 mm |
| CENTUM Isoliersattel für Rollenlager 813 Iso  50, roh | 149arae0813 | 70 mm | 915 mm | 4250928434548 | 52.26 kg | 52.26 kg | Isoliersattel 813 70 x 10 mm | für Iso 50 mm roh | roh | 813 mm | 15 mm  [stored 0.0492126 ft] | 10 mm | M20x70 | 50 mm |
| CENTUM Isoliersattel für Rollenlager 813 Iso  80, fvz | 149afah0813 | 70 mm | 975 mm | 4250928433640 | 57.50 kg | 57.50 kg | Isoliersattel 813 70 x 10 mm | für Iso 80 mm fsv | feuerstückverzinkt | 813 mm | 15 mm  [stored 0.0492126 ft] | 10 mm | M20x70 | 80 mm |
| CENTUM Isoliersattel für Rollenlager 813 Iso  80, gvz | 149agah0813 | 70 mm | 975 mm | 4250928434142 | 55.65 kg | 55.65 kg | Isoliersattel 813 70 x 10 mm | für Iso 80 mm gvz | galvanisch verzinkt | 813 mm | 15 mm  [stored 0.0492126 ft] | 10 mm | M20x70 | 80 mm |
| CENTUM Isoliersattel für Rollenlager 813 Iso  80, roh | 149arah0813 | 70 mm | 975 mm | 4250928434647 | 55.65 kg | 55.65 kg | Isoliersattel 813 70 x 10 mm | für Iso 80 mm roh | roh | 813 mm | 15 mm  [stored 0.0492126 ft] | 10 mm | M20x70 | 80 mm |
| CENTUM Isoliersattel für Rollenlager 813 Iso 100, fvz | 149afak0813 | 70 mm | 1.015 mm | 4250928433749 | 59.83 kg | 59.83 kg | Isoliersattel 813 70 x 10 mm | für Iso 100 mm fsv | feuerstückverzinkt | 813 mm | 15 mm  [stored 0.0492126 ft] | 10 mm | M20x70 | 100 mm |
| CENTUM Isoliersattel für Rollenlager 813 Iso 120, gvz | 149agam0813 | 70 mm | 1.055 mm | 4250928434340 | 60.19 kg | 60.19 kg | Isoliersattel 813 70 x 10 mm | für Iso 120 mm gvz | galvanisch verzinkt | 813 mm | 15 mm  [stored 0.0492126 ft] | 10 mm | M20x70 | 120 mm |
| CENTUM Isoliersattel für Rollenlager 813 Iso 100, gvz | 149agak0813 | 70 mm | 1.015 mm | 4250928434241 | 57.93 kg | 57.93 kg | Isoliersattel 813 70 x 10 mm | für Iso 100 mm gvz | galvanisch verzinkt | 813 mm | 15 mm  [stored 0.0492126 ft] | 10 mm | M20x70 | 100 mm |
| CENTUM Isoliersattel für Rollenlager 813 Iso 100, roh | 149arak0813 | 70 mm | 1.015 mm | 4250928434746 | 57.93 kg | 57.93 kg | Isoliersattel 813 70 x 10 mm | für Iso 100 mm roh | roh | 813 mm | 15 mm  [stored 0.0492126 ft] | 10 mm | M20x70 | 100 mm |
| CENTUM Isoliersattel für Rollenlager 813 Iso 120, fvz | 149afam0813 | 70 mm | 1.055 mm | 4250928433848 | 62.14 kg | 62.14 kg | Isoliersattel 813 70 x 10 mm | für Iso 120 mm fsv | feuerstückverzinkt | 813 mm | 15 mm  [stored 0.0492126 ft] | 10 mm | M20x70 | 120 mm |
| CENTUM Isoliersattel für Rollenlager 813 Iso 120, roh | 149aram0813 | 70 mm | 1.055 mm | 4250928434845 | 60.19 kg | 60.19 kg | Isoliersattel 813 70 x 10 mm | für Iso 120 mm roh | roh | 813 mm | 15 mm  [stored 0.0492126 ft] | 10 mm | M20x70 | 120 mm |
| CENTUM Isoliersattel für Rollenlager 813 Iso 150, fvz | 149afap0813 | 70 mm | 1.115 mm | 4250928433947 | 65.64 kg | 65.64 kg | Isoliersattel 813 70 x 10 mm | für Iso 150 mm fsv | feuerstückverzinkt | 813 mm | 15 mm  [stored 0.0492126 ft] | 10 mm | M20x70 | 150 mm |
| CENTUM Isoliersattel für Rollenlager 813 Iso 150, gvz | 149agap0813 | 70 mm | 1.115 mm | 4250928434449 | 63.60 kg | 63.60 kg | Isoliersattel 813 70 x 10 mm | für Iso 150 mm gvz | galvanisch verzinkt | 813 mm | 15 mm  [stored 0.0492126 ft] | 10 mm | M20x70 | 150 mm |
| CENTUM Isoliersattel für Rollenlager 813 Iso 150, roh | 149arap0813 | 70 mm | 1.115 mm | 4250928434944 | 63.60 kg | 63.60 kg | Isoliersattel 813 70 x 10 mm | für Iso 150 mm roh | roh | 813 mm | 15 mm  [stored 0.0492126 ft] | 10 mm | M20x70 | 150 mm |

note: [stored X ft] marks values corroborated as IEEE doubles in the binary element streams (Revit-internal decimal feet)
